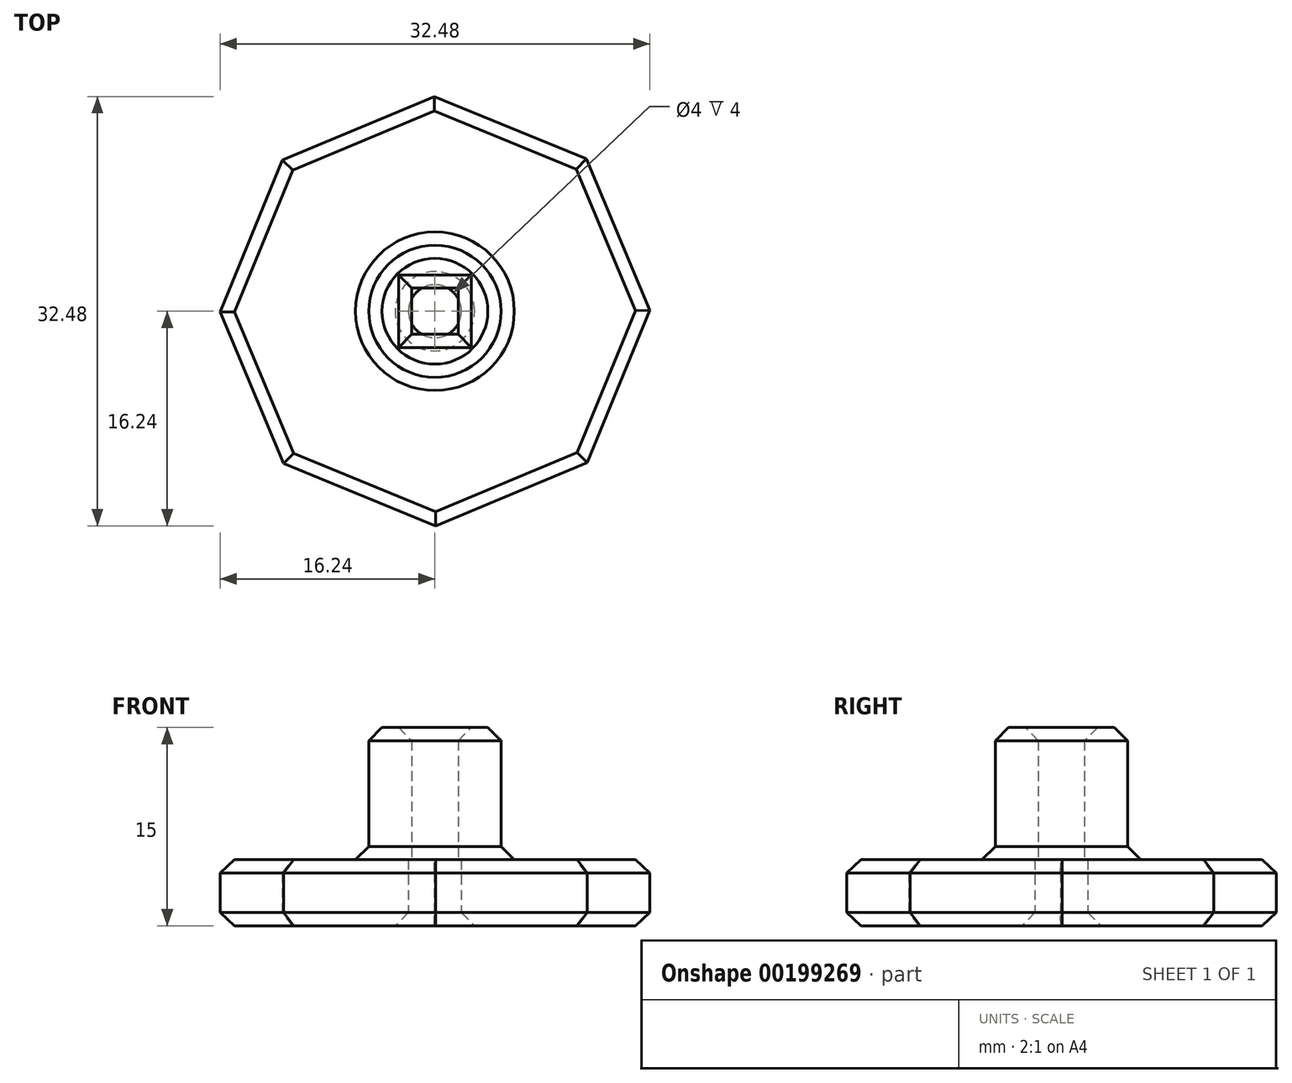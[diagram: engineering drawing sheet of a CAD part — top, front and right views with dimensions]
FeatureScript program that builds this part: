
annotation { "Feature Type Name" : "Feature", "Feature Type Description" : "" }
export const myFeature = defineFeature(function(context is Context, id is Id, definition is map)
    precondition{}
    {
        {
            var Q0;
            Q0=qCreatedBy(makeId("Top.planeOp"),FACE);
            var sketch = newSketch(context, id + "F0", { "sketchPlane" : qUnion([Q0])});
            skCircle(sketch, "E0.cCircle", {"center": v(0, 0) * mm, "radius": 15 * mm, "construction": true});
            skLineSegment(sketch, "E0.0", {"start": v(11.44, 11.52) * mm, "end": v(16.24, 0.06) * mm});
            skLineSegment(sketch, "E0.1", {"start": v(16.24, 0.06) * mm, "end": v(11.52, -11.44) * mm});
            skLineSegment(sketch, "E0.2", {"start": v(11.52, -11.44) * mm, "end": v(0.06, -16.24) * mm});
            skLineSegment(sketch, "E0.3", {"start": v(0.06, -16.24) * mm, "end": v(-11.44, -11.52) * mm});
            skLineSegment(sketch, "E0.4", {"start": v(-11.44, -11.52) * mm, "end": v(-16.24, -0.06) * mm});
            skLineSegment(sketch, "E0.5", {"start": v(-16.24, -0.06) * mm, "end": v(-11.52, 11.44) * mm});
            skLineSegment(sketch, "E0.6", {"start": v(-11.52, 11.44) * mm, "end": v(-0.06, 16.24) * mm});
            skLineSegment(sketch, "E0.7", {"start": v(-0.06, 16.24) * mm, "end": v(11.44, 11.52) * mm});
            skPoint(sketch, "E0.0.midPoint", {"position": v(13.84, 5.8) * mm});
            skCircle(sketch, "E1", {"center": v(0, 0) * mm, "radius": 2 * mm});
            skSolve(sketch);
        }
        {
            var Q0;
            Q0=makeQuery(id+"F0.imprint","IMPRINT",FACE,{"disambiguationData":[TD([[makeQuery(id+"F0.imprint","IMPRINT",EDGE,{"derivedFrom":sQuery(id+"F0.wireOp",EDGE,"E0.0")}),-1.0]])]});
            extrude(context, id + "F1", {"entities" : qUnion([Q0]), "depth" : 5 * mm});
        }
        {
            var Q0;
            Q0=makeQuery(id+"F1.opExtrude","CAP_FACE",FACE,{"disambiguationData":[OSD([sQuery(id+"F0.wireOp",EDGE,"E0.0"),sQuery(id+"F0.wireOp",EDGE,"E0.1"),sQuery(id+"F0.wireOp",EDGE,"E0.2"),sQuery(id+"F0.wireOp",EDGE,"E0.3"),sQuery(id+"F0.wireOp",EDGE,"E0.4"),sQuery(id+"F0.wireOp",EDGE,"E0.5"),sQuery(id+"F0.wireOp",EDGE,"E0.6"),sQuery(id+"F0.wireOp",EDGE,"E0.7"),sQuery(id+"F0.wireOp",EDGE,"E1")])],"isStart":false});
            var sketch = newSketch(context, id + "F2", { "sketchPlane" : qUnion([Q0])});
            skCircle(sketch, "E2", {"center": v(0, 0) * mm, "radius": 5 * mm});
            skLineSegment(sketch, "E3.bottom", {"start": v(1.75, 1.75) * mm, "end": v(-1.75, 1.75) * mm});
            skLineSegment(sketch, "E3.top", {"start": v(1.75, -1.75) * mm, "end": v(-1.75, -1.75) * mm});
            skLineSegment(sketch, "E3.left", {"start": v(1.75, 1.75) * mm, "end": v(1.75, -1.75) * mm});
            skLineSegment(sketch, "E3.right", {"start": v(-1.75, 1.75) * mm, "end": v(-1.75, -1.75) * mm});
            skSolve(sketch);
        }
        {
            var Q0;
            Q0=makeQuery(id+"F2.imprint","IMPRINT",FACE,{"disambiguationData":[TD([[makeQuery(id+"F2.imprint","IMPRINT",EDGE,{"derivedFrom":sQuery(id+"F2.wireOp",EDGE,"E2")}),1.0]])]});
            var Q1;
            {var subQ0=sQuery(id+"F2.wireOp",EDGE,"E3.bottom");var subQ1=makeQuery(id+"F1.opExtrude","CAP_EDGE",EDGE,{"disambiguationData":[OSD([sQuery(id+"F0.wireOp",EDGE,"E1")])],"isStart":false});var subQ2=makeQuery(id+"F2.imprint","INTERSECT",VERTEX,{"disambiguationData":[OD(0.0)],"derivedFrom":[subQ1,subQ0]});Q1=makeQuery(id+"F2.imprint","IMPRINT",FACE,{"disambiguationData":[TD([[makeQuery(id+"F2.imprint","IMPRINT",EDGE,{"disambiguationData":[TD([[subQ2,-1.0]])],"derivedFrom":subQ0}),-1.0]])]});}
            var Q2;
            {var subQ0=sQuery(id+"F2.wireOp",EDGE,"E3.left");var subQ1=makeQuery(id+"F1.opExtrude","CAP_EDGE",EDGE,{"disambiguationData":[OSD([sQuery(id+"F0.wireOp",EDGE,"E1")])],"isStart":false});var subQ2=makeQuery(id+"F2.imprint","INTERSECT",VERTEX,{"disambiguationData":[OD(0.0)],"derivedFrom":[subQ1,subQ0]});Q2=makeQuery(id+"F2.imprint","IMPRINT",FACE,{"disambiguationData":[TD([[makeQuery(id+"F2.imprint","IMPRINT",EDGE,{"disambiguationData":[TD([[subQ2,-1.0]])],"derivedFrom":subQ0}),1.0]])]});}
            var Q3;
            {var subQ0=sQuery(id+"F2.wireOp",EDGE,"E3.top");var subQ1=makeQuery(id+"F1.opExtrude","CAP_EDGE",EDGE,{"disambiguationData":[OSD([sQuery(id+"F0.wireOp",EDGE,"E1")])],"isStart":false});var subQ2=makeQuery(id+"F2.imprint","INTERSECT",VERTEX,{"disambiguationData":[OD(0.0)],"derivedFrom":[subQ1,subQ0]});Q3=makeQuery(id+"F2.imprint","IMPRINT",FACE,{"disambiguationData":[TD([[makeQuery(id+"F2.imprint","IMPRINT",EDGE,{"disambiguationData":[TD([[subQ2,-1.0]])],"derivedFrom":subQ0}),1.0]])]});}
            var Q4;
            {var subQ0=sQuery(id+"F2.wireOp",EDGE,"E3.right");var subQ1=makeQuery(id+"F1.opExtrude","CAP_EDGE",EDGE,{"disambiguationData":[OSD([sQuery(id+"F0.wireOp",EDGE,"E1")])],"isStart":false});var subQ2=makeQuery(id+"F2.imprint","INTERSECT",VERTEX,{"disambiguationData":[OD(0.0)],"derivedFrom":[subQ1,subQ0]});Q4=makeQuery(id+"F2.imprint","IMPRINT",FACE,{"disambiguationData":[TD([[makeQuery(id+"F2.imprint","IMPRINT",EDGE,{"disambiguationData":[TD([[subQ2,-1.0]])],"derivedFrom":subQ0}),-1.0]])]});}
            extrude(context, id + "F3", {"entities" : qUnion([Q0, Q1, Q2, Q3, Q4]), "operationType" : NewBodyOperationType.ADD, "depth" : 10 * mm});
        }
        {
            var Q0;
            Q0=makeQuery(id+"F3.opExtrude","CAP_FACE",FACE,{"disambiguationData":[OSD([sQuery(id+"F2.wireOp",EDGE,"E2"),sQuery(id+"F2.wireOp",EDGE,"E3.bottom"),sQuery(id+"F2.wireOp",EDGE,"E3.top"),sQuery(id+"F2.wireOp",EDGE,"E3.left"),sQuery(id+"F2.wireOp",EDGE,"E3.right")])],"isStart":false});
            var Q1;
            Q1=makeQuery(id+"F3.opExtrude","CAP_EDGE",EDGE,{"disambiguationData":[OSD([sQuery(id+"F2.wireOp",EDGE,"E2")])],"isStart":true});
            var Q2;
            Q2=makeQuery(id+"F1.opExtrude","CAP_EDGE",EDGE,{"disambiguationData":[OSD([sQuery(id+"F0.wireOp",EDGE,"E0.1")])],"isStart":false});
            var Q3;
            Q3=makeQuery(id+"F1.opExtrude","CAP_EDGE",EDGE,{"disambiguationData":[OSD([sQuery(id+"F0.wireOp",EDGE,"E0.0")])],"isStart":false});
            var Q4;
            {var subQ0=sQuery(id+"F0.wireOp",EDGE,"E0.3");var subQ1=sQuery(id+"F0.wireOp",EDGE,"E0.2");var subQ2=sQuery(id+"F0.wireOp",EDGE,"E0.1");var subQ3=sQuery(id+"F0.wireOp",EDGE,"E0.0");var subQ4=sQuery(id+"F0.wireOp",EDGE,"E0.4");var subQ5=sQuery(id+"F0.wireOp",EDGE,"E0.5");var subQ6=sQuery(id+"F0.wireOp",EDGE,"E0.6");var subQ7=sQuery(id+"F0.wireOp",EDGE,"E0.7");Q4=makeQuery(id+"F3.boolean.opBoolean","SPLIT",FACE,{"disambiguationData":[TD([makeQuery(id+"F1.opExtrude","SWEPT_FACE",FACE,{"disambiguationData":[OSD([subQ3])]}),makeQuery(id+"F1.opExtrude","SWEPT_FACE",FACE,{"disambiguationData":[OSD([subQ2])]}),makeQuery(id+"F1.opExtrude","SWEPT_FACE",FACE,{"disambiguationData":[OSD([subQ1])]}),makeQuery(id+"F1.opExtrude","SWEPT_FACE",FACE,{"disambiguationData":[OSD([subQ0])]}),makeQuery(id+"F1.opExtrude","SWEPT_FACE",FACE,{"disambiguationData":[OSD([subQ4])]}),makeQuery(id+"F1.opExtrude","SWEPT_FACE",FACE,{"disambiguationData":[OSD([subQ5])]}),makeQuery(id+"F1.opExtrude","SWEPT_FACE",FACE,{"disambiguationData":[OSD([subQ6])]}),makeQuery(id+"F1.opExtrude","SWEPT_FACE",FACE,{"disambiguationData":[OSD([subQ7])]}),makeQuery(id+"F3.opExtrude","SWEPT_FACE",FACE,{"disambiguationData":[OSD([sQuery(id+"F2.wireOp",EDGE,"E2")])]})])],"derivedFrom":makeQuery(id+"F1.opExtrude","CAP_FACE",FACE,{"disambiguationData":[OSD([subQ3,subQ2,subQ1,subQ0,subQ4,subQ5,subQ6,subQ7,sQuery(id+"F0.wireOp",EDGE,"E1")])],"isStart":false})});}
            var Q5;
            Q5=makeQuery(id+"F1.opExtrude","CAP_FACE",FACE,{"disambiguationData":[OSD([sQuery(id+"F0.wireOp",EDGE,"E0.0"),sQuery(id+"F0.wireOp",EDGE,"E0.1"),sQuery(id+"F0.wireOp",EDGE,"E0.2"),sQuery(id+"F0.wireOp",EDGE,"E0.3"),sQuery(id+"F0.wireOp",EDGE,"E0.4"),sQuery(id+"F0.wireOp",EDGE,"E0.5"),sQuery(id+"F0.wireOp",EDGE,"E0.6"),sQuery(id+"F0.wireOp",EDGE,"E0.7"),sQuery(id+"F0.wireOp",EDGE,"E1")])],"isStart":true});
            chamfer(context, id + "F4", {"entities" : qUnion([Q0, Q1, Q2, Q3, Q4, Q5]), "width" : 1 * mm, "tangentPropagation" : true});
        }
    });
